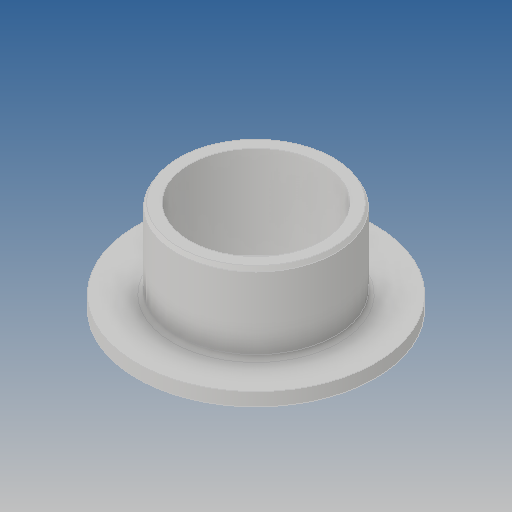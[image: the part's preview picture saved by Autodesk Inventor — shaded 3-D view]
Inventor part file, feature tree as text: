
AUTODESK INVENTOR PART (.ipt)
format: ipt  version: 2018 (Build 220112000, 112)  size: 128,000 bytes
history: native  units: mm
features: fillet x1
ambient origin geometry x8: Origin, YZ Plane, XZ Plane, XY Plane, X Axis, Y Axis, Z Axis, Center Point
bodies: Solid1 (feature_tree)
feature tree (1):
  fillet  "Fillet1"  [1 undecoded]
note: 1 required parameter value undecoded (feature->parameter linkage not recoverable at this tier; creation-order binding heuristic only, values carry confidence <= 0.55)
